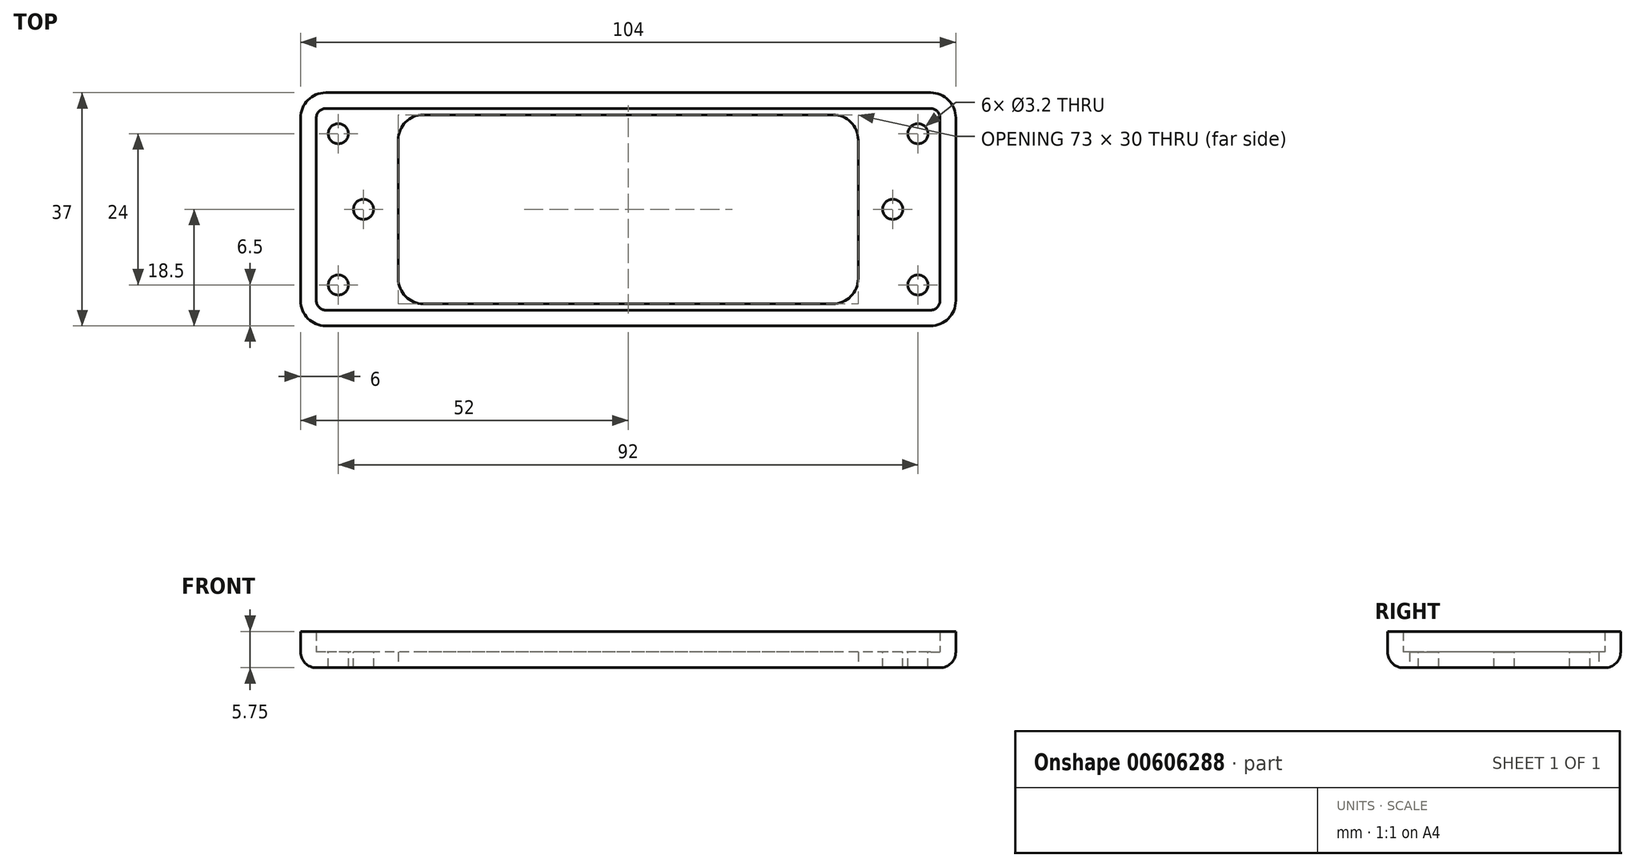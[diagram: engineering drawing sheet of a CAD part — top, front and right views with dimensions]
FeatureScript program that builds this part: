
annotation { "Feature Type Name" : "Feature", "Feature Type Description" : "" }
export const myFeature = defineFeature(function(context is Context, id is Id, definition is map)
    precondition{}
    {
        {
            var Q0;
            Q0=qCreatedBy(makeId("Top.planeOp"),FACE);
            var sketch = newSketch(context, id + "F0", { "sketchPlane" : qUnion([Q0])});
            skLineSegment(sketch, "E0.bottom", {"start": v(48, 18.5) * mm, "end": v(-48, 18.5) * mm});
            skLineSegment(sketch, "E0.top", {"start": v(48, -18.5) * mm, "end": v(-48, -18.5) * mm});
            skLineSegment(sketch, "E0.left", {"start": v(52, 14.5) * mm, "end": v(52, -14.5) * mm});
            skLineSegment(sketch, "E0.right", {"start": v(-52, 14.5) * mm, "end": v(-52, -14.5) * mm});
            skPoint(sketch, "E0.middle", {"position": v(0, 0) * mm});
            skLineSegment(sketch, "E1.bottom", {"start": v(32.5, 15) * mm, "end": v(-32.5, 15) * mm});
            skLineSegment(sketch, "E1.top", {"start": v(32.5, -15) * mm, "end": v(-32.5, -15) * mm});
            skLineSegment(sketch, "E1.left", {"start": v(36.5, 11) * mm, "end": v(36.5, -11) * mm});
            skLineSegment(sketch, "E1.right", {"start": v(-36.5, 11) * mm, "end": v(-36.5, -11) * mm});
            skPoint(sketch, "E2.visualSharp", {"position": v(-52, 18.5) * mm});
            skArc(sketch, "E2.filletArc", {"start": v(-48, 18.5) * mm, "mid": v(-50.83, 17.33) * mm, "end": v(-52, 14.5) * mm});
            skPoint(sketch, "E3.visualSharp", {"position": v(-52, -18.5) * mm});
            skArc(sketch, "E3.filletArc", {"start": v(-52, -14.5) * mm, "mid": v(-50.83, -17.33) * mm, "end": v(-48, -18.5) * mm});
            skPoint(sketch, "E4.visualSharp", {"position": v(-36.5, -15) * mm});
            skArc(sketch, "E4.filletArc", {"start": v(-36.5, -11) * mm, "mid": v(-35.33, -13.83) * mm, "end": v(-32.5, -15) * mm});
            skPoint(sketch, "E5.visualSharp", {"position": v(-36.5, 15) * mm});
            skArc(sketch, "E5.filletArc", {"start": v(-32.5, 15) * mm, "mid": v(-35.33, 13.83) * mm, "end": v(-36.5, 11) * mm});
            skPoint(sketch, "E6.visualSharp", {"position": v(36.5, 15) * mm});
            skArc(sketch, "E6.filletArc", {"start": v(36.5, 11) * mm, "mid": v(35.33, 13.83) * mm, "end": v(32.5, 15) * mm});
            skPoint(sketch, "E7.visualSharp", {"position": v(36.5, -15) * mm});
            skArc(sketch, "E7.filletArc", {"start": v(32.5, -15) * mm, "mid": v(35.33, -13.83) * mm, "end": v(36.5, -11) * mm});
            skPoint(sketch, "E8.visualSharp", {"position": v(52, 18.5) * mm});
            skArc(sketch, "E8.filletArc", {"start": v(52, 14.5) * mm, "mid": v(50.83, 17.33) * mm, "end": v(48, 18.5) * mm});
            skPoint(sketch, "E9.visualSharp", {"position": v(52, -18.5) * mm});
            skArc(sketch, "E9.filletArc", {"start": v(48, -18.5) * mm, "mid": v(50.83, -17.33) * mm, "end": v(52, -14.5) * mm});
            skSolve(sketch);
        }
        {
            var Q0;
            Q0 = qSketchRegion(id + "F0", true);
            extrude(context, id + "F1", {"entities" : qUnion([Q0]), "depth" : 2.5 * mm, "offsetDistance" : 25 * mm});
        }
        {
            var Q0;
            Q0=makeQuery(id+"F1.opExtrude","CAP_FACE",FACE,{"disambiguationData":[OSD([sQuery(id+"F0.wireOp",EDGE,"E0.bottom"),sQuery(id+"F0.wireOp",EDGE,"E0.top"),sQuery(id+"F0.wireOp",EDGE,"E0.left"),sQuery(id+"F0.wireOp",EDGE,"E0.right"),sQuery(id+"F0.wireOp",EDGE,"E1.bottom"),sQuery(id+"F0.wireOp",EDGE,"E1.top"),sQuery(id+"F0.wireOp",EDGE,"E1.left"),sQuery(id+"F0.wireOp",EDGE,"E1.right"),sQuery(id+"F0.wireOp",EDGE,"E2.filletArc"),sQuery(id+"F0.wireOp",EDGE,"E3.filletArc"),sQuery(id+"F0.wireOp",EDGE,"E4.filletArc"),sQuery(id+"F0.wireOp",EDGE,"E5.filletArc"),sQuery(id+"F0.wireOp",EDGE,"E6.filletArc"),sQuery(id+"F0.wireOp",EDGE,"E7.filletArc"),sQuery(id+"F0.wireOp",EDGE,"E8.filletArc"),sQuery(id+"F0.wireOp",EDGE,"E9.filletArc")])],"isStart":false});
            var sketch = newSketch(context, id + "F2", { "sketchPlane" : qUnion([Q0])});
            skLineSegment(sketch, "E10.bottom", {"start": v(46, 12) * mm, "end": v(-46, 12) * mm, "construction": true});
            skLineSegment(sketch, "E10.top", {"start": v(46, -12) * mm, "end": v(-46, -12) * mm, "construction": true});
            skLineSegment(sketch, "E10.left", {"start": v(46, 12) * mm, "end": v(46, -12) * mm, "construction": true});
            skLineSegment(sketch, "E10.right", {"start": v(-46, 12) * mm, "end": v(-46, -12) * mm, "construction": true});
            skPoint(sketch, "E10.middle", {"position": v(0, 0) * mm});
            skCircle(sketch, "E11", {"center": v(-46, 12) * mm, "radius": 1.6 * mm});
            skCircle(sketch, "E12", {"center": v(46, 12) * mm, "radius": 1.6 * mm});
            skCircle(sketch, "E13", {"center": v(46, -12) * mm, "radius": 1.6 * mm});
            skCircle(sketch, "E14", {"center": v(-46, -12) * mm, "radius": 1.6 * mm});
            skLineSegment(sketch, "E15", {"start": v(-42, 0) * mm, "end": v(42, 0) * mm, "construction": true});
            skCircle(sketch, "E16", {"center": v(-42, 0) * mm, "radius": 1.6 * mm});
            skCircle(sketch, "E17", {"center": v(42, 0) * mm, "radius": 1.6 * mm});
            skSolve(sketch);
        }
        {
            var Q0;
            Q0 = qSketchRegion(id + "F2", true);
            extrude(context, id + "F3", {"entities" : qUnion([Q0]), "operationType" : NewBodyOperationType.REMOVE, "endBound" : BoundingType.THROUGH_ALL, "oppositeDirection" : true, "depth" : 25 * mm, "offsetDistance" : 25 * mm});
        }
        {
            var Q0;
            Q0=makeQuery(id+"F1.opExtrude","CAP_FACE",FACE,{"disambiguationData":[OSD([sQuery(id+"F0.wireOp",EDGE,"E0.bottom"),sQuery(id+"F0.wireOp",EDGE,"E0.top"),sQuery(id+"F0.wireOp",EDGE,"E0.left"),sQuery(id+"F0.wireOp",EDGE,"E0.right"),sQuery(id+"F0.wireOp",EDGE,"E1.bottom"),sQuery(id+"F0.wireOp",EDGE,"E1.top"),sQuery(id+"F0.wireOp",EDGE,"E1.left"),sQuery(id+"F0.wireOp",EDGE,"E1.right"),sQuery(id+"F0.wireOp",EDGE,"E2.filletArc"),sQuery(id+"F0.wireOp",EDGE,"E3.filletArc"),sQuery(id+"F0.wireOp",EDGE,"E4.filletArc"),sQuery(id+"F0.wireOp",EDGE,"E5.filletArc"),sQuery(id+"F0.wireOp",EDGE,"E6.filletArc"),sQuery(id+"F0.wireOp",EDGE,"E7.filletArc"),sQuery(id+"F0.wireOp",EDGE,"E8.filletArc"),sQuery(id+"F0.wireOp",EDGE,"E9.filletArc")])],"isStart":false});
            var sketch = newSketch(context, id + "F4", { "sketchPlane" : qUnion([Q0])});
            skArc(sketch, "E18.0", {"start": v(-48, 18.5) * mm, "mid": v(-50.83, 17.33) * mm, "end": v(-52, 14.5) * mm});
            skLineSegment(sketch, "E18.1", {"start": v(-52, 14.5) * mm, "end": v(-52, -14.5) * mm});
            skArc(sketch, "E18.2", {"start": v(-52, -14.5) * mm, "mid": v(-50.83, -17.33) * mm, "end": v(-48, -18.5) * mm});
            skLineSegment(sketch, "E18.3", {"start": v(48, -18.5) * mm, "end": v(-48, -18.5) * mm});
            skArc(sketch, "E18.4", {"start": v(48, -18.5) * mm, "mid": v(50.83, -17.33) * mm, "end": v(52, -14.5) * mm});
            skLineSegment(sketch, "E18.5", {"start": v(52, 14.5) * mm, "end": v(52, -14.5) * mm});
            skArc(sketch, "E18.6", {"start": v(52, 14.5) * mm, "mid": v(50.83, 17.33) * mm, "end": v(48, 18.5) * mm});
            skLineSegment(sketch, "E18.7", {"start": v(48, 18.5) * mm, "end": v(-48, 18.5) * mm});
            skLineSegment(sketch, "E19.0", {"start": v(-49.5, 14.5) * mm, "end": v(-49.5, -14.5) * mm});
            skArc(sketch, "E19.1", {"start": v(-48, 16) * mm, "mid": v(-49.06, 15.56) * mm, "end": v(-49.5, 14.5) * mm});
            skArc(sketch, "E19.2", {"start": v(-49.5, -14.5) * mm, "mid": v(-49.06, -15.56) * mm, "end": v(-48, -16) * mm});
            skLineSegment(sketch, "E19.3", {"start": v(48, 16) * mm, "end": v(-48, 16) * mm});
            skLineSegment(sketch, "E19.4", {"start": v(48, -16) * mm, "end": v(-48, -16) * mm});
            skArc(sketch, "E19.5", {"start": v(48, -16) * mm, "mid": v(49.06, -15.56) * mm, "end": v(49.5, -14.5) * mm});
            skLineSegment(sketch, "E19.6", {"start": v(49.5, 14.5) * mm, "end": v(49.5, -14.5) * mm});
            skArc(sketch, "E19.7", {"start": v(49.5, 14.5) * mm, "mid": v(49.06, 15.56) * mm, "end": v(48, 16) * mm});
            skSolve(sketch);
        }
        {
            var Q0;
            Q0 = qSketchRegion(id + "F4", true);
            extrude(context, id + "F5", {"entities" : qUnion([Q0]), "operationType" : NewBodyOperationType.ADD, "depth" : 3.25 * mm, "offsetDistance" : 25 * mm});
        }
        {
            var Q0;
            Q0=makeQuery(id+"F1.opExtrude","CAP_EDGE",EDGE,{"disambiguationData":[OSD([sQuery(id+"F0.wireOp",EDGE,"E2.filletArc")])],"isStart":true});
            var Q1;
            Q1=makeQuery(id+"F1.opExtrude","CAP_EDGE",EDGE,{"disambiguationData":[OSD([sQuery(id+"F0.wireOp",EDGE,"E0.bottom")])],"isStart":true});
            var Q2;
            Q2=makeQuery(id+"F1.opExtrude","CAP_EDGE",EDGE,{"disambiguationData":[OSD([sQuery(id+"F0.wireOp",EDGE,"E0.right")])],"isStart":true});
            var Q3;
            Q3=makeQuery(id+"F1.opExtrude","CAP_EDGE",EDGE,{"disambiguationData":[OSD([sQuery(id+"F0.wireOp",EDGE,"E3.filletArc")])],"isStart":true});
            var Q4;
            Q4=makeQuery(id+"F1.opExtrude","CAP_EDGE",EDGE,{"disambiguationData":[OSD([sQuery(id+"F0.wireOp",EDGE,"E0.top")])],"isStart":true});
            var Q5;
            Q5=makeQuery(id+"F1.opExtrude","CAP_EDGE",EDGE,{"disambiguationData":[OSD([sQuery(id+"F0.wireOp",EDGE,"E9.filletArc")])],"isStart":true});
            var Q6;
            Q6=makeQuery(id+"F1.opExtrude","CAP_EDGE",EDGE,{"disambiguationData":[OSD([sQuery(id+"F0.wireOp",EDGE,"E0.left")])],"isStart":true});
            var Q7;
            Q7=makeQuery(id+"F1.opExtrude","CAP_EDGE",EDGE,{"disambiguationData":[OSD([sQuery(id+"F0.wireOp",EDGE,"E8.filletArc")])],"isStart":true});
            fillet(context, id + "F6", {"entities" : qUnion([Q0, Q1, Q2, Q3, Q4, Q5, Q6, Q7]), "radius" : 2.5 * mm, "tangentPropagation" : true, "allowEdgeOverflow" : false});
        }
    });
